# Revit family: Trane_TVR_Outdoor_4TVH0192(210)FE000AA_380~415V(50_60Hz)
name_source: partatom
category: Equipamento mecânico
units: mm (PartAtom-declared; Revit-internal decimal feet)

## family parameters
Com base no plano de trabalho = Não
Compartilhado = Não
Corte com vazios quando carregada = Não
Cota do conector redondo = Utilizar diâmetro
Número OmniClass = 23.75.00.00
Ponto de cálculo do ambiente = Não
Sempre na vertical = Sim
Tipo de parte = Normal
Título OmniClass = Climate Control (HVAC)

## types (2) — shared parameters
Air Flow = 17000.000 m³/h
Casing color = White
Compressor = 2
Condensation = Air
Depth = 825  [stored 2.70669 ft]
Descrição = High efficiency air cooled
Fabricante = Trane
Gas = R410A
Gas pipe = 31.8  [stored 0.104331 ft]
Height = 1635  [stored 5.36417 ft]
Installation = Outdoor installation
Liquid pipe = 19.1  [stored 0.062664 ft]
Machine material = Galvanized Steel
Net Weight = 344.00 kg
Power supply = 380V 3Ph~60Hz
Series = ULTRA S
URL = https://www.trane.com
Width = 1340
clearance access behind = 1000  [stored 3.28084 ft]
clearance access front = 1000  [stored 3.28084 ft]
clearance access left = 1000  [stored 3.28084 ft]
clearance access right = 1000  [stored 3.28084 ft]

## per-type parameters (varying)
| type | Cooling Capacity | Cooling Power Input | Heating Capacity | Heating Power Input | Maximum Fuse Amps | Minimum Circuit Amps |
| 4TVH0192FE000AA | 56.000 kW | 14.660 kW | 56.000 kW | 13.020 kW | 50 A | 46 A |
| 4TVH0210FE000AA | 61.500 kW | 18.520 kW | 61.500 kW | 16.490 kW | 63 A | 48 A |

note: column(s) folded — value = type name in every type: Modelo

note: [stored X ft] marks values corroborated as IEEE doubles in the binary element streams (Revit-internal decimal feet)

## geometry (parser evidence)
native form markers: Blend x6, Sweep x39
no freeform markers — native parametric forms only
